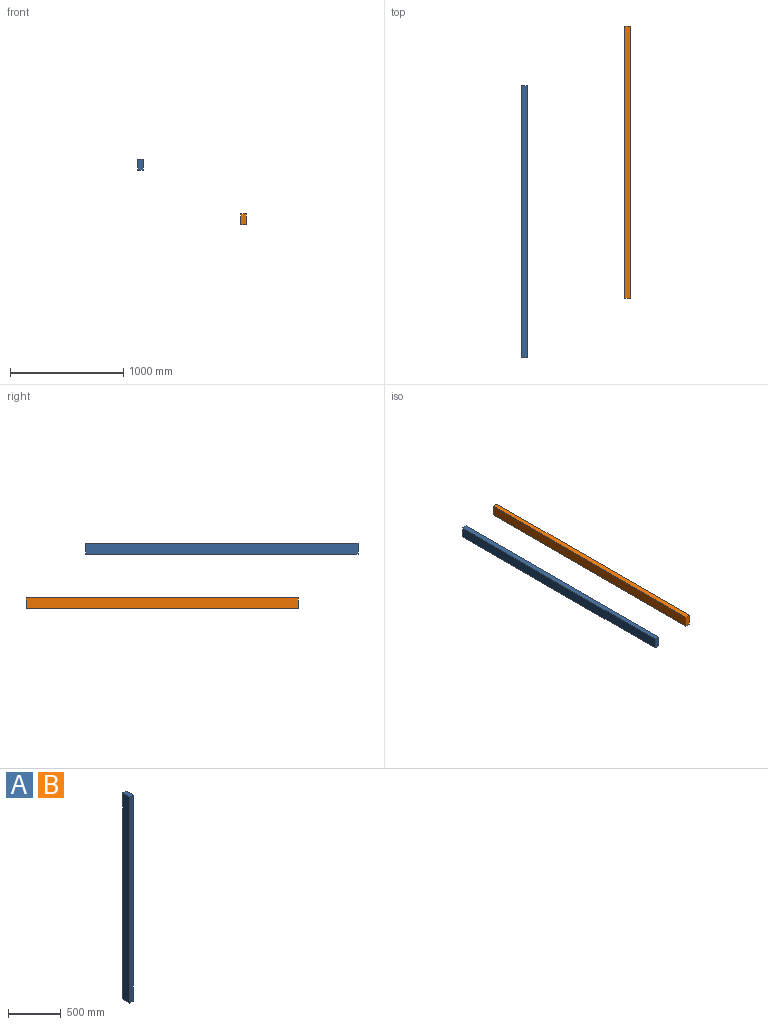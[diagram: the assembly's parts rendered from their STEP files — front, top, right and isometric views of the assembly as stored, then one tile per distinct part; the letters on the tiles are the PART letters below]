
ASSEMBLY  parts=2 mates=1
PART A: 6 faces, bbox 45x95x2400 mm
  f0: plane 2400x95mm, normal (1,0,0), area 228000mm2, adj f1,f3,f4,f5
  f1: plane 2400x45mm, normal (0,1,0), area 108000mm2, adj f0,f2,f4,f5
  f2: plane 2400x95mm, normal (-1,0,0), area 228000mm2, adj f1,f3,f4,f5
  f3: plane 2400x45mm, normal (0,-1,0), area 108000mm2, adj f0,f2,f4,f5
  f4: plane 95x45mm, normal (0,0,1), area 4275mm2, adj f0,f1,f2,f3
  f5: plane 95x45mm, normal (0,0,-1), area 4275mm2, adj f0,f1,f2,f3
PART B: same geometry as A
PLACE A rot(axis=(0,0.71,0.71),180deg) t=(-7324.08,47.57,-2141.26)mm
PLACE B rot(axis=(0,0.71,0.71),180deg) t=(-6416.01,573.47,-2622.34)mm
MATE parallel A.f0 <-> B.f2  axis (-1,0,0) through (-7346.58,1247.57,-2141.26)mm
